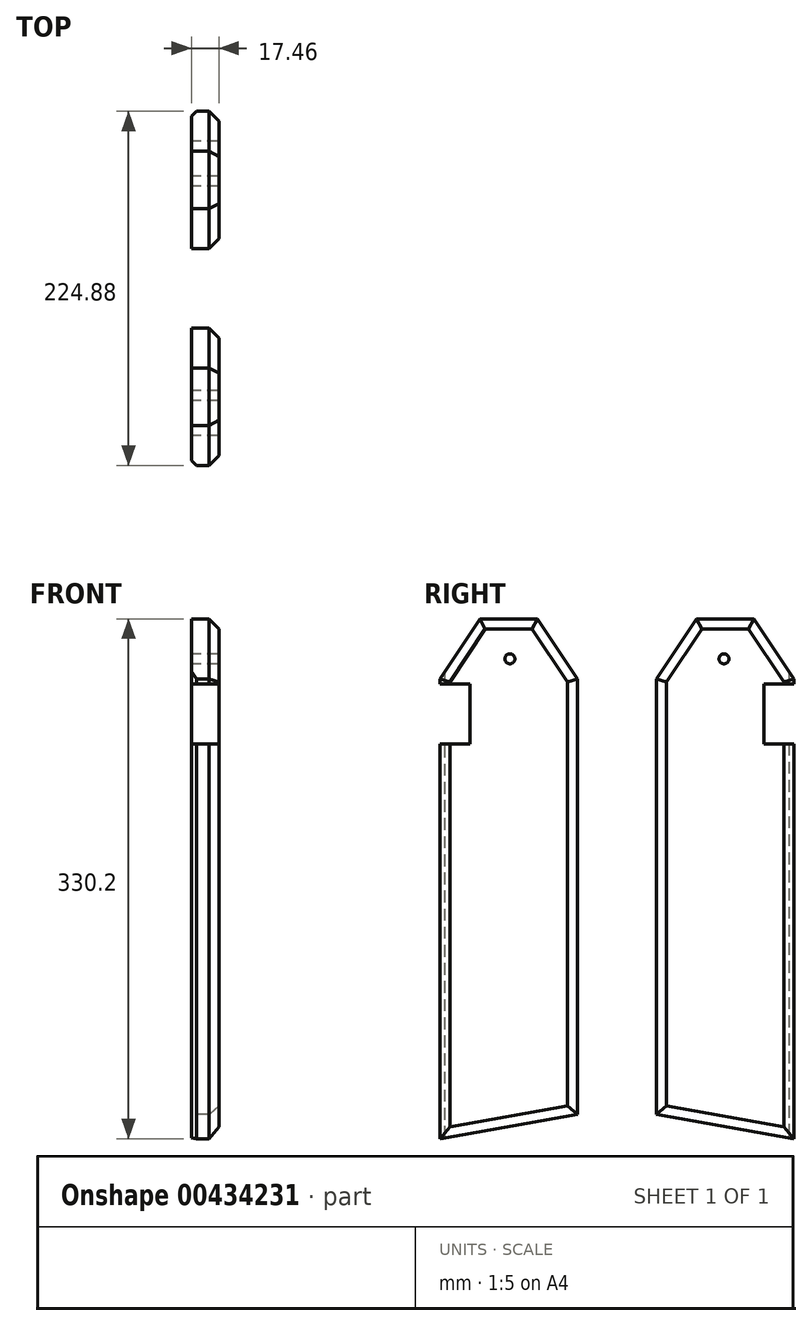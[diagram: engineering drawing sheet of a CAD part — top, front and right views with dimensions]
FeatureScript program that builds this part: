
annotation { "Feature Type Name" : "Feature", "Feature Type Description" : "" }
export const myFeature = defineFeature(function(context is Context, id is Id, definition is map)
    precondition{}
    {
        {
            var Q0;
            Q0=qCreatedBy(makeId("Right.planeOp"),FACE);
            var sketch = newSketch(context, id + "F0", { "sketchPlane" : qUnion([Q0])});
            skLineSegment(sketch, "E0.bottom", {"start": v(0, 0) * mm, "end": v(-87.31, 0) * mm, "construction": true});
            skLineSegment(sketch, "E0.top", {"start": v(0, -330.2) * mm, "end": v(-87.31, -330.2) * mm, "construction": true});
            skLineSegment(sketch, "E0.left", {"start": v(0, -38.1) * mm, "end": v(0, -314.8) * mm});
            skLineSegment(sketch, "E0.right", {"start": v(-87.31, -38.1) * mm, "end": v(-87.31, -41.27) * mm});
            skLineSegment(sketch, "E1", {"start": v(-87.31, -330.2) * mm, "end": v(0, -314.8) * mm});
            skLineSegment(sketch, "E2", {"start": v(0, -330.2) * mm, "end": v(0, -314.8) * mm, "construction": true});
            skCircle(sketch, "E3", {"center": v(-42.86, -25.4) * mm, "radius": 3.18 * mm});
            skLineSegment(sketch, "E4", {"start": v(-87.31, -38.1) * mm, "end": v(-61.91, 0) * mm});
            skLineSegment(sketch, "E5", {"start": v(-61.91, 0) * mm, "end": v(-25.4, 0) * mm});
            skLineSegment(sketch, "E6", {"start": v(-25.4, 0) * mm, "end": v(0, -38.1) * mm});
            skLineSegment(sketch, "E7", {"start": v(-87.31, -38.1) * mm, "end": v(-87.31, 0) * mm, "construction": true});
            skLineSegment(sketch, "E8", {"start": v(0, 0) * mm, "end": v(0, -38.1) * mm, "construction": true});
            skLineSegment(sketch, "E9", {"start": v(25.13, 0) * mm, "end": v(25.13, -330.2) * mm, "construction": true});
            skCircle(sketch, "E10.MirrorC", {"center": v(93.12, -25.4) * mm, "radius": 3.18 * mm});
            skLineSegment(sketch, "E11.MirrorCS", {"start": v(112.17, 0) * mm, "end": v(75.66, 0) * mm});
            skLineSegment(sketch, "E12.MirrorCS", {"start": v(50.26, -38.1) * mm, "end": v(50.26, -314.8) * mm});
            skLineSegment(sketch, "E13.MirrorCS", {"start": v(137.57, -330.2) * mm, "end": v(50.26, -314.8) * mm});
            skLineSegment(sketch, "E14.MirrorCS", {"start": v(50.26, -330.2) * mm, "end": v(50.26, -314.8) * mm, "construction": true});
            skLineSegment(sketch, "E15.MirrorCS", {"start": v(137.57, -38.1) * mm, "end": v(112.17, 0) * mm});
            skLineSegment(sketch, "E16.MirrorCS", {"start": v(75.66, 0) * mm, "end": v(50.26, -38.1) * mm});
            skLineSegment(sketch, "E17.MirrorCS", {"start": v(137.57, -38.1) * mm, "end": v(137.57, 0) * mm, "construction": true});
            skLineSegment(sketch, "E18.MirrorCS", {"start": v(50.26, 0) * mm, "end": v(50.26, -38.1) * mm, "construction": true});
            skLineSegment(sketch, "E19.MirrorCS", {"start": v(50.26, 0) * mm, "end": v(137.57, 0) * mm, "construction": true});
            skLineSegment(sketch, "E20.MirrorCS", {"start": v(50.26, -330.2) * mm, "end": v(137.57, -330.2) * mm, "construction": true});
            skLineSegment(sketch, "E21.MirrorCS", {"start": v(50.26, -38.1) * mm, "end": v(137.57, -38.1) * mm, "construction": true});
            skLineSegment(sketch, "E22", {"start": v(-87.31, -38.1) * mm, "end": v(0, -38.1) * mm, "construction": true});
            skLineSegment(sketch, "E23", {"start": v(-87.31, -41.27) * mm, "end": v(-68.26, -41.27) * mm});
            skLineSegment(sketch, "E24", {"start": v(-68.26, -41.27) * mm, "end": v(-68.26, -79.37) * mm});
            skLineSegment(sketch, "E25", {"start": v(-68.26, -79.37) * mm, "end": v(-87.31, -79.37) * mm});
            skLineSegment(sketch, "E26.trimOffspring", {"start": v(-87.31, -79.37) * mm, "end": v(-87.31, -330.2) * mm});
            skLineSegment(sketch, "E27.MirrorCS", {"start": v(137.57, -41.27) * mm, "end": v(118.52, -41.27) * mm});
            skLineSegment(sketch, "E28.MirrorCS", {"start": v(118.52, -41.27) * mm, "end": v(118.52, -79.37) * mm});
            skLineSegment(sketch, "E29.MirrorCS", {"start": v(118.52, -79.37) * mm, "end": v(137.57, -79.37) * mm});
            skLineSegment(sketch, "E30.MirrorCS", {"start": v(137.57, -38.1) * mm, "end": v(137.57, -41.27) * mm});
            skLineSegment(sketch, "E31.MirrorCS", {"start": v(137.57, -79.37) * mm, "end": v(137.57, -330.2) * mm});
            skSolve(sketch);
        }
        {
            var Q0;
            Q0 = qSketchRegion(id + "F0", true);
            extrude(context, id + "F1", {"entities" : qUnion([Q0]), "depth" : 17.46 * mm});
        }
        {
            var Q0;
            Q0=makeQuery(id+"F1.opExtrude","CAP_EDGE",EDGE,{"disambiguationData":[OSD([sQuery(id+"F0.wireOp",EDGE,"E4")])],"isStart":false});
            var Q1;
            Q1=makeQuery(id+"F1.opExtrude","CAP_EDGE",EDGE,{"disambiguationData":[OSD([sQuery(id+"F0.wireOp",EDGE,"E5")])],"isStart":false});
            var Q2;
            Q2=makeQuery(id+"F1.opExtrude","CAP_EDGE",EDGE,{"disambiguationData":[OSD([sQuery(id+"F0.wireOp",EDGE,"E6")])],"isStart":false});
            var Q3;
            Q3=makeQuery(id+"F1.opExtrude","CAP_EDGE",EDGE,{"disambiguationData":[OSD([sQuery(id+"F0.wireOp",EDGE,"E0.left")])],"isStart":false});
            var Q4;
            Q4=makeQuery(id+"F1.opExtrude","CAP_EDGE",EDGE,{"disambiguationData":[OSD([sQuery(id+"F0.wireOp",EDGE,"E0.right")])],"isStart":false});
            var Q5;
            Q5=makeQuery(id+"F1.opExtrude","CAP_EDGE",EDGE,{"disambiguationData":[OSD([sQuery(id+"F0.wireOp",EDGE,"E1")])],"isStart":false});
            var Q6;
            Q6=makeQuery(id+"F1.opExtrude","CAP_EDGE",EDGE,{"disambiguationData":[OSD([sQuery(id+"F0.wireOp",EDGE,"E13.MirrorCS")])],"isStart":false});
            var Q7;
            Q7=makeQuery(id+"F1.opExtrude","CAP_EDGE",EDGE,{"disambiguationData":[OSD([sQuery(id+"F0.wireOp",EDGE,"E12.MirrorCS")])],"isStart":false});
            var Q8;
            Q8=makeQuery(id+"F1.opExtrude","CAP_EDGE",EDGE,{"disambiguationData":[OSD([sQuery(id+"F0.wireOp",EDGE,"f23bf8ea-3d05-4a58-b799-b011d6196e993.MirrorCS")])],"isStart":false});
            var Q9;
            Q9=makeQuery(id+"F1.opExtrude","CAP_EDGE",EDGE,{"disambiguationData":[OSD([sQuery(id+"F0.wireOp",EDGE,"E15.MirrorCS")])],"isStart":false});
            var Q10;
            Q10=makeQuery(id+"F1.opExtrude","CAP_EDGE",EDGE,{"disambiguationData":[OSD([sQuery(id+"F0.wireOp",EDGE,"E11.MirrorCS")])],"isStart":false});
            var Q11;
            Q11=makeQuery(id+"F1.opExtrude","CAP_EDGE",EDGE,{"disambiguationData":[OSD([sQuery(id+"F0.wireOp",EDGE,"E16.MirrorCS")])],"isStart":false});
            var Q12;
            Q12=makeQuery(id+"F1.opExtrude","CAP_EDGE",EDGE,{"disambiguationData":[OSD([sQuery(id+"F0.wireOp",EDGE,"E26.trimOffspring")])],"isStart":false});
            var Q13;
            Q13=makeQuery(id+"F1.opExtrude","CAP_EDGE",EDGE,{"disambiguationData":[OSD([sQuery(id+"F0.wireOp",EDGE,"E31.MirrorCS")])],"isStart":false});
            var Q14;
            Q14=makeQuery(id+"F1.opExtrude","CAP_EDGE",EDGE,{"disambiguationData":[OSD([sQuery(id+"F0.wireOp",EDGE,"E30.MirrorCS")])],"isStart":false});
            chamfer(context, id + "F2", {"entities" : qUnion([Q0, Q1, Q2, Q3, Q4, Q5, Q6, Q7, Q8, Q9, Q10, Q11, Q12, Q13, Q14]), "width" : 6.35 * mm, "tangentPropagation" : true});
        }
        {
            var Q0;
            Q0=makeQuery(id+"F1.opExtrude","CAP_EDGE",EDGE,{"disambiguationData":[OSD([sQuery(id+"F0.wireOp",EDGE,"E31.MirrorCS")])],"isStart":true});
            var Q1;
            Q1=makeQuery(id+"F1.opExtrude","CAP_EDGE",EDGE,{"disambiguationData":[OSD([sQuery(id+"F0.wireOp",EDGE,"E30.MirrorCS")])],"isStart":true});
            var Q2;
            Q2=makeQuery(id+"F1.opExtrude","CAP_EDGE",EDGE,{"disambiguationData":[OSD([sQuery(id+"F0.wireOp",EDGE,"E0.right")])],"isStart":true});
            var Q3;
            Q3=makeQuery(id+"F1.opExtrude","CAP_EDGE",EDGE,{"disambiguationData":[OSD([sQuery(id+"F0.wireOp",EDGE,"E26.trimOffspring")])],"isStart":true});
            chamfer(context, id + "F3", {"entities" : qUnion([Q0, Q1, Q2, Q3]), "width" : 3.17 * mm, "tangentPropagation" : true});
        }
    });
